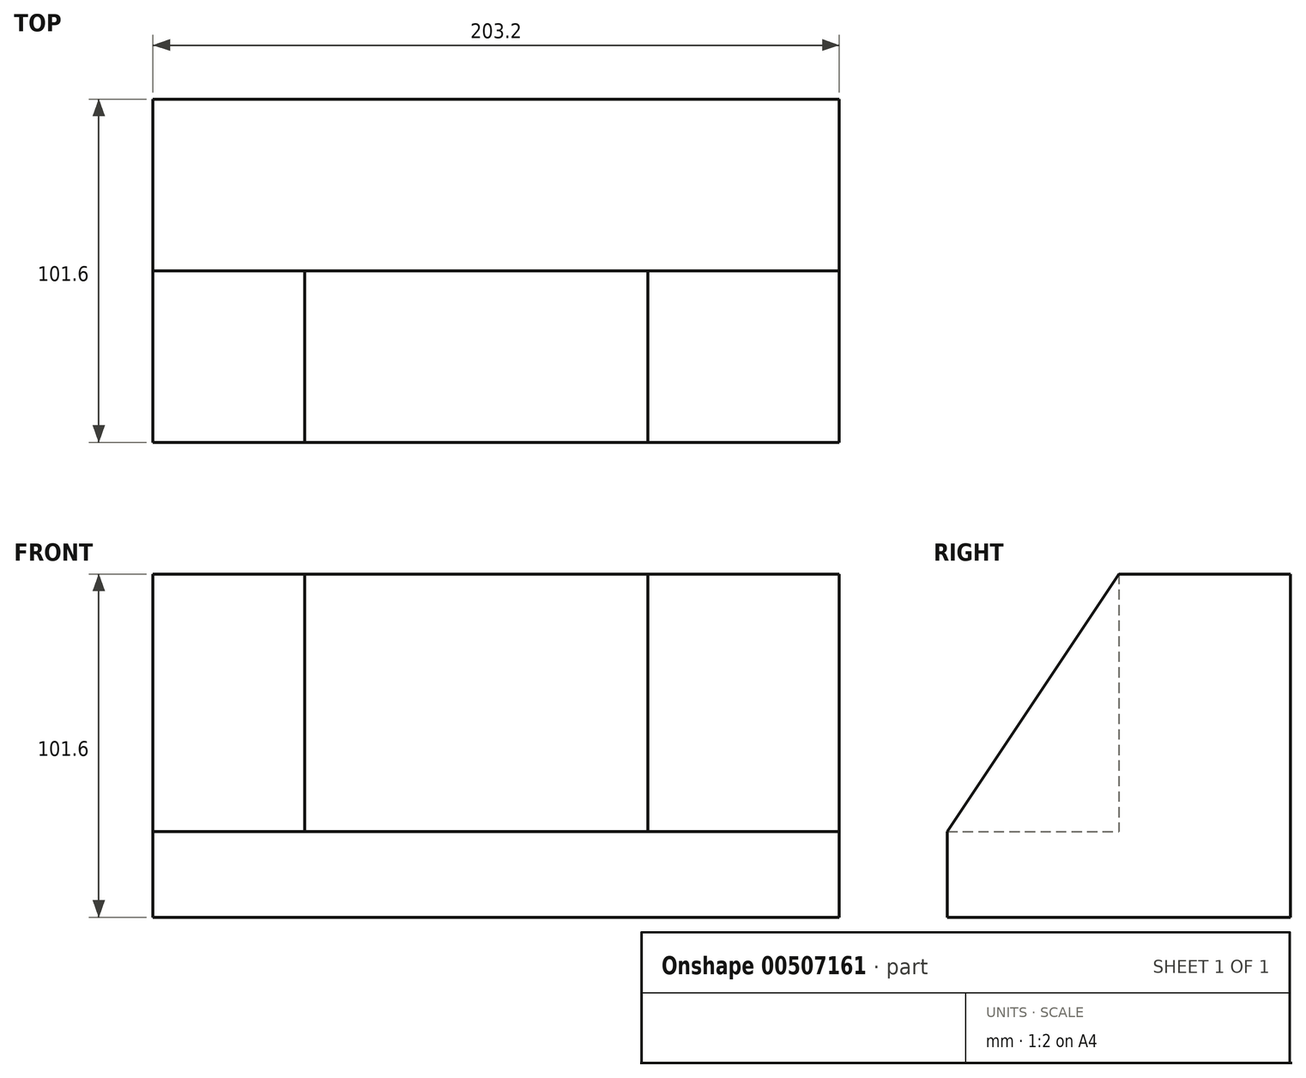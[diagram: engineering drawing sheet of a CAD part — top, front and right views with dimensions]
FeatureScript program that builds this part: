
annotation { "Feature Type Name" : "Feature", "Feature Type Description" : "" }
export const myFeature = defineFeature(function(context is Context, id is Id, definition is map)
    precondition{}
    {
        {
            var Q0;
            Q0=qCreatedBy(makeId("Top.planeOp"),FACE);
            var sketch = newSketch(context, id + "F0", { "sketchPlane" : qUnion([Q0])});
            skLineSegment(sketch, "E0", {"start": v(-64.5, 73.72) * mm, "end": v(-64.5, 22.92) * mm});
            skLineSegment(sketch, "E1", {"start": v(-64.5, 22.92) * mm, "end": v(138.7, 22.92) * mm});
            skLineSegment(sketch, "E2", {"start": v(-64.5, 73.72) * mm, "end": v(138.7, 73.72) * mm});
            skLineSegment(sketch, "E3", {"start": v(138.7, 73.72) * mm, "end": v(138.7, 22.92) * mm});
            skSolve(sketch);
        }
        {
            var Q0;
            Q0 = qSketchRegion(id + "F0", true);
            extrude(context, id + "F1", {"entities" : qUnion([Q0]), "depth" : 101.6 * mm});
        }
        {
            var Q0;
            Q0=makeQuery(id+"F1.opExtrude","SWEPT_FACE",FACE,{"disambiguationData":[OSD([sQuery(id+"F0.wireOp",EDGE,"E0")])]});
            var sketch = newSketch(context, id + "F2", { "sketchPlane" : qUnion([Q0])});
            skLineSegment(sketch, "E4", {"start": v(-73.72, 0) * mm, "end": v(27.88, 0) * mm});
            skLineSegment(sketch, "E5", {"start": v(27.88, 0) * mm, "end": v(27.88, 25.4) * mm});
            skLineSegment(sketch, "E6", {"start": v(27.88, 25.4) * mm, "end": v(-73.72, 25.4) * mm});
            skLineSegment(sketch, "E7", {"start": v(-73.72, 25.4) * mm, "end": v(-73.72, 0) * mm});
            skSolve(sketch);
        }
        {
            var Q0;
            Q0 = qSketchRegion(id + "F2", true);
            extrude(context, id + "F3", {"entities" : qUnion([Q0]), "operationType" : NewBodyOperationType.ADD, "oppositeDirection" : true, "depth" : 203.2 * mm});
        }
        {
            var Q0;
            Q0=makeQuery(id+"F3.boolean.opBoolean","MERGE",FACE,{"derivedFrom":[makeQuery(id+"F1.opExtrude","SWEPT_FACE",FACE,{"disambiguationData":[OSD([sQuery(id+"F0.wireOp",EDGE,"E3")])]}),makeQuery(id+"F3.opExtrude","CAP_FACE",FACE,{"disambiguationData":[OSD([sQuery(id+"F2.wireOp",EDGE,"E4"),sQuery(id+"F2.wireOp",EDGE,"E5"),sQuery(id+"F2.wireOp",EDGE,"E6"),sQuery(id+"F2.wireOp",EDGE,"E7")])],"isStart":false})]});
            var sketch = newSketch(context, id + "F4", { "sketchPlane" : qUnion([Q0])});
            skLineSegment(sketch, "E8", {"start": v(-27.88, 25.4) * mm, "end": v(22.92, 101.6) * mm});
            skLineSegment(sketch, "E9", {"start": v(22.92, 101.6) * mm, "end": v(22.92, 25.4) * mm});
            skLineSegment(sketch, "E10", {"start": v(22.92, 25.4) * mm, "end": v(-27.88, 25.4) * mm});
            skSolve(sketch);
        }
        {
            var Q0;
            Q0 = qSketchRegion(id + "F4", true);
            extrude(context, id + "F5", {"entities" : qUnion([Q0]), "operationType" : NewBodyOperationType.ADD, "oppositeDirection" : true, "depth" : 203.2 * mm});
        }
        {
            var Q0;
            Q0=qCreatedBy(makeId("Top.planeOp"),FACE);
            var sketch = newSketch(context, id + "F6", { "sketchPlane" : qUnion([Q0])});
            skLineSegment(sketch, "E11", {"start": v(-19.53, 22.92) * mm, "end": v(-19.53, -27.88) * mm});
            skLineSegment(sketch, "E12", {"start": v(-19.53, -27.88) * mm, "end": v(82.07, -27.88) * mm});
            skLineSegment(sketch, "E13", {"start": v(82.07, -27.88) * mm, "end": v(82.07, 22.92) * mm});
            skLineSegment(sketch, "E14", {"start": v(82.07, 22.92) * mm, "end": v(-19.53, 22.92) * mm});
            skSolve(sketch);
        }
        {
            var Q0;
            Q0 = qSketchRegion(id + "F6", true);
            extrude(context, id + "F7", {"entities" : qUnion([Q0]), "operationType" : NewBodyOperationType.REMOVE, "depth" : 101.6 * mm});
        }
        {
            var Q0;
            Q0=makeQuery(id+"F7.boolean.opBoolean","COPY",FACE,{"derivedFrom":makeQuery(id+"F7.opExtrude","SWEPT_FACE",FACE,{"disambiguationData":[OSD([sQuery(id+"F6.wireOp",EDGE,"E11")])]})});
            var sketch = newSketch(context, id + "F8", { "sketchPlane" : qUnion([Q0])});
            skLineSegment(sketch, "E15", {"start": v(-27.88, 25.4) * mm, "end": v(22.92, 25.4) * mm});
            skLineSegment(sketch, "E16", {"start": v(22.92, 25.4) * mm, "end": v(22.92, 0) * mm});
            skLineSegment(sketch, "E17", {"start": v(22.92, 0) * mm, "end": v(-27.88, 0) * mm});
            skLineSegment(sketch, "E18", {"start": v(-27.88, 0) * mm, "end": v(-27.88, 25.4) * mm});
            skSolve(sketch);
        }
        {
            var Q0;
            Q0 = qSketchRegion(id + "F8", true);
            extrude(context, id + "F9", {"entities" : qUnion([Q0]), "operationType" : NewBodyOperationType.ADD, "depth" : 101.6 * mm});
        }
    });
